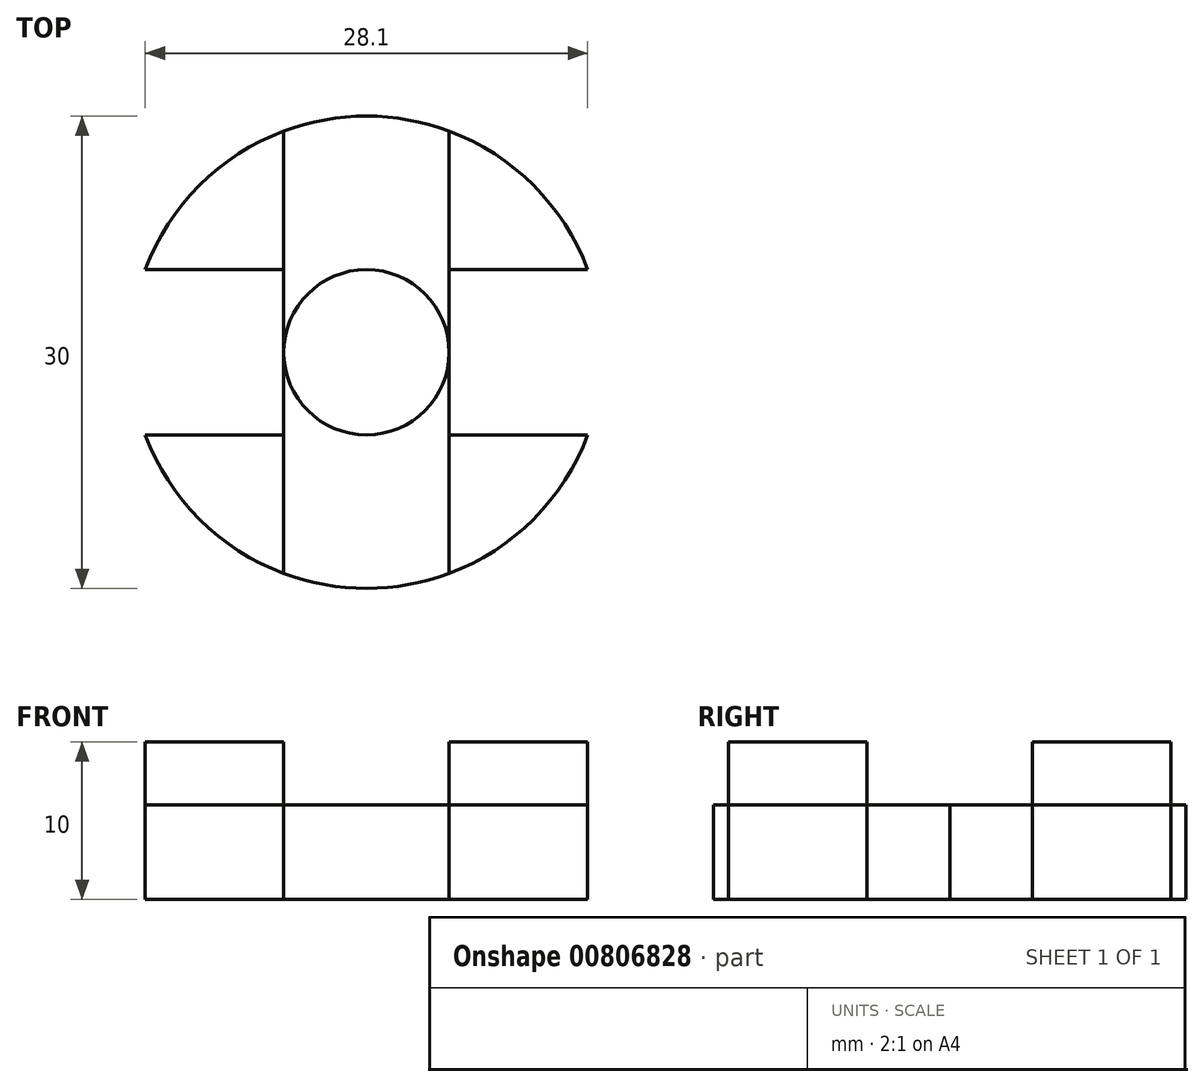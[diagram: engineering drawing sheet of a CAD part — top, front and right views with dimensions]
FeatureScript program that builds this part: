
annotation { "Feature Type Name" : "Feature", "Feature Type Description" : "" }
export const myFeature = defineFeature(function(context is Context, id is Id, definition is map)
    precondition{}
    {
        {
            var Q0;
            Q0=qCreatedBy(makeId("Top.planeOp"),FACE);
            var sketch = newSketch(context, id + "F0", { "sketchPlane" : qUnion([Q0])});
            skCircle(sketch, "E0", {"center": v(0, 0) * mm, "radius": 15 * mm});
            skCircle(sketch, "E1", {"center": v(0, 0) * mm, "radius": 5.25 * mm});
            skLineSegment(sketch, "E2.bottom", {"start": v(5.25, 21.3) * mm, "end": v(-5.25, 21.3) * mm});
            skLineSegment(sketch, "E2.top", {"start": v(5.25, -21.3) * mm, "end": v(-5.25, -21.3) * mm});
            skLineSegment(sketch, "E2.left", {"start": v(5.25, 21.3) * mm, "end": v(5.25, -21.3) * mm});
            skLineSegment(sketch, "E2.right", {"start": v(-5.25, 21.3) * mm, "end": v(-5.25, -21.3) * mm});
            skLineSegment(sketch, "E3.bottom", {"start": v(25.07, 5.25) * mm, "end": v(-25.07, 5.25) * mm});
            skLineSegment(sketch, "E3.top", {"start": v(25.07, -5.25) * mm, "end": v(-25.07, -5.25) * mm});
            skLineSegment(sketch, "E3.left", {"start": v(25.07, 5.25) * mm, "end": v(25.07, -5.25) * mm});
            skLineSegment(sketch, "E3.right", {"start": v(-25.07, 5.25) * mm, "end": v(-25.07, -5.25) * mm});
            skSolve(sketch);
        }
        {
            var Q0;
            Q0=makeQuery(id+"F0.imprint","IMPRINT",FACE,{"disambiguationData":[TD([[makeQuery(id+"F0.imprint","IMPRINT",EDGE,{"derivedFrom":sQuery(id+"F0.wireOp",EDGE,"E0")}),1.0]])]});
            var Q1;
            {var subQ0=sQuery(id+"F0.wireOp",EDGE,"E3.bottom");var subQ1=sQuery(id+"F0.wireOp",EDGE,"E0");var subQ2=makeQuery(id+"F0.imprint","INTERSECT",VERTEX,{"disambiguationData":[OD(1.0)],"derivedFrom":[subQ1,subQ0]});Q1=makeQuery(id+"F0.imprint","IMPRINT",FACE,{"disambiguationData":[TD([[makeQuery(id+"F0.imprint","IMPRINT",EDGE,{"disambiguationData":[TD([[subQ2,-1.0]])],"derivedFrom":subQ1}),1.0]])]});}
            var Q2;
            {var subQ0=sQuery(id+"F0.wireOp",EDGE,"E2.right");var subQ1=sQuery(id+"F0.wireOp",EDGE,"E0");var subQ2=makeQuery(id+"F0.imprint","INTERSECT",VERTEX,{"disambiguationData":[OD(1.0)],"derivedFrom":[subQ1,subQ0]});Q2=makeQuery(id+"F0.imprint","IMPRINT",FACE,{"disambiguationData":[TD([[makeQuery(id+"F0.imprint","IMPRINT",EDGE,{"disambiguationData":[TD([[subQ2,-1.0]])],"derivedFrom":subQ1}),1.0]])]});}
            var Q3;
            {var subQ0=sQuery(id+"F0.wireOp",EDGE,"E3.bottom");var subQ1=sQuery(id+"F0.wireOp",EDGE,"E0");var subQ2=makeQuery(id+"F0.imprint","INTERSECT",VERTEX,{"disambiguationData":[OD(0.0)],"derivedFrom":[subQ1,subQ0]});Q3=makeQuery(id+"F0.imprint","IMPRINT",FACE,{"disambiguationData":[TD([[makeQuery(id+"F0.imprint","IMPRINT",EDGE,{"disambiguationData":[TD([[subQ2,1.0]])],"derivedFrom":subQ1}),1.0]])]});}
            var Q4;
            {var subQ0=sQuery(id+"F0.wireOp",EDGE,"E2.left");var subQ1=sQuery(id+"F0.wireOp",EDGE,"E0");var subQ2=makeQuery(id+"F0.imprint","INTERSECT",VERTEX,{"disambiguationData":[OD(0.0)],"derivedFrom":[subQ1,subQ0]});Q4=makeQuery(id+"F0.imprint","IMPRINT",FACE,{"disambiguationData":[TD([[makeQuery(id+"F0.imprint","IMPRINT",EDGE,{"disambiguationData":[TD([[subQ2,-1.0]])],"derivedFrom":subQ1}),1.0]])]});}
            var Q5;
            Q5=makeQuery(id+"F0.imprint","IMPRINT",FACE,{"disambiguationData":[TD([[makeQuery(id+"F0.imprint","IMPRINT",EDGE,{"derivedFrom":sQuery(id+"F0.wireOp",EDGE,"E1")}),-1.0]])]});
            extrude(context, id + "F1", {"entities" : qUnion([Q0, Q1, Q2, Q3, Q4, Q5]), "depth" : 6 * mm, "offsetDistance" : 25 * mm});
        }
        {
            var Q0;
            {var subQ0=sQuery(id+"F0.wireOp",EDGE,"E2.right");var subQ1=sQuery(id+"F0.wireOp",EDGE,"E0");var subQ2=makeQuery(id+"F0.imprint","INTERSECT",VERTEX,{"disambiguationData":[OD(0.0)],"derivedFrom":[subQ1,subQ0]});Q0=makeQuery(id+"F0.imprint","IMPRINT",FACE,{"disambiguationData":[TD([[makeQuery(id+"F0.imprint","IMPRINT",EDGE,{"disambiguationData":[TD([[subQ2,-1.0]])],"derivedFrom":subQ1}),1.0]])]});}
            var Q1;
            {var subQ0=sQuery(id+"F0.wireOp",EDGE,"E3.top");var subQ1=sQuery(id+"F0.wireOp",EDGE,"E0");var subQ2=makeQuery(id+"F0.imprint","INTERSECT",VERTEX,{"disambiguationData":[OD(0.0)],"derivedFrom":[subQ1,subQ0]});Q1=makeQuery(id+"F0.imprint","IMPRINT",FACE,{"disambiguationData":[TD([[makeQuery(id+"F0.imprint","IMPRINT",EDGE,{"disambiguationData":[TD([[subQ2,-1.0]])],"derivedFrom":subQ1}),1.0]])]});}
            var Q2;
            {var subQ0=sQuery(id+"F0.wireOp",EDGE,"E2.left");var subQ1=sQuery(id+"F0.wireOp",EDGE,"E0");var subQ2=makeQuery(id+"F0.imprint","INTERSECT",VERTEX,{"disambiguationData":[OD(1.0)],"derivedFrom":[subQ1,subQ0]});Q2=makeQuery(id+"F0.imprint","IMPRINT",FACE,{"disambiguationData":[TD([[makeQuery(id+"F0.imprint","IMPRINT",EDGE,{"disambiguationData":[TD([[subQ2,-1.0]])],"derivedFrom":subQ1}),1.0]])]});}
            var Q3;
            {var subQ0=sQuery(id+"F0.wireOp",EDGE,"E2.left");var subQ1=sQuery(id+"F0.wireOp",EDGE,"E0");var subQ2=makeQuery(id+"F0.imprint","INTERSECT",VERTEX,{"disambiguationData":[OD(0.0)],"derivedFrom":[subQ1,subQ0]});Q3=makeQuery(id+"F0.imprint","IMPRINT",FACE,{"disambiguationData":[TD([[makeQuery(id+"F0.imprint","IMPRINT",EDGE,{"disambiguationData":[TD([[subQ2,1.0]])],"derivedFrom":subQ1}),1.0]])]});}
            extrude(context, id + "F2", {"entities" : qUnion([Q0, Q1, Q2, Q3]), "depth" : 10 * mm, "offsetDistance" : 25 * mm});
        }
    });
